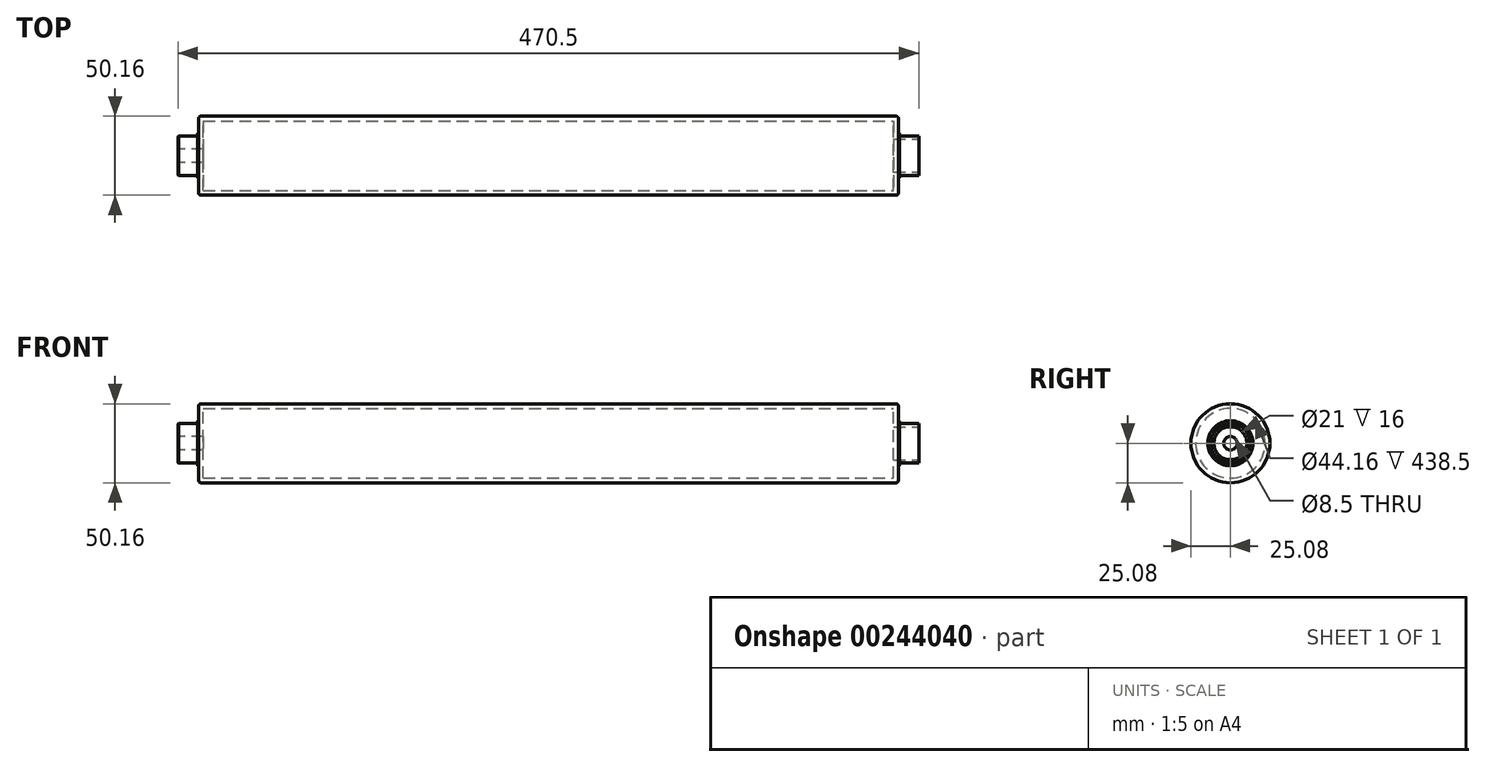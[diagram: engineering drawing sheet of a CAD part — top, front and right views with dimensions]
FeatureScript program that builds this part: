
annotation { "Feature Type Name" : "Feature", "Feature Type Description" : "" }
export const myFeature = defineFeature(function(context is Context, id is Id, definition is map)
    precondition{}
    {
        {
            var Q0;
            Q0=qCreatedBy(makeId("Front.planeOp"),FACE);
            var sketch = newSketch(context, id + "F0", { "sketchPlane" : qUnion([Q0])});
            skLineSegment(sketch, "E0", {"start": v(0, -12.5) * mm, "end": v(12.4, -12.5) * mm});
            skLineSegment(sketch, "E1", {"start": v(12.4, -12.5) * mm, "end": v(12.4, -14.3) * mm});
            skLineSegment(sketch, "E2", {"start": v(12.4, -14.3) * mm, "end": v(12.8, -14.3) * mm});
            skLineSegment(sketch, "E3", {"start": v(13, -14.5) * mm, "end": v(13, -23.58) * mm});
            skLineSegment(sketch, "E4", {"start": v(14.5, -25.08) * mm, "end": v(456, -25.08) * mm});
            skLineSegment(sketch, "E5", {"start": v(457.5, -23.58) * mm, "end": v(457.5, -14.5) * mm});
            skLineSegment(sketch, "E6", {"start": v(457.7, -14.3) * mm, "end": v(458.1, -14.3) * mm});
            skLineSegment(sketch, "E7", {"start": v(458.1, -14.3) * mm, "end": v(458.1, -12.5) * mm});
            skLineSegment(sketch, "E8", {"start": v(458.1, -12.5) * mm, "end": v(470.5, -12.5) * mm});
            skLineSegment(sketch, "E9", {"start": v(470.5, -12.5) * mm, "end": v(470.5, -10.5) * mm});
            skLineSegment(sketch, "E10", {"start": v(470.5, -10.5) * mm, "end": v(454.5, -10.5) * mm});
            skLineSegment(sketch, "E11", {"start": v(454.5, -10.5) * mm, "end": v(454.5, -22.08) * mm});
            skLineSegment(sketch, "E12", {"start": v(454.5, -22.08) * mm, "end": v(16, -22.08) * mm});
            skLineSegment(sketch, "E13", {"start": v(16, -22.08) * mm, "end": v(16, 0) * mm});
            skLineSegment(sketch, "E14", {"start": v(16, 0) * mm, "end": v(0, 0) * mm});
            skLineSegment(sketch, "E15", {"start": v(0, 0) * mm, "end": v(0, -12.5) * mm});
            skPoint(sketch, "E16.visualSharp", {"position": v(13, -14.3) * mm});
            skArc(sketch, "E16.filletArc", {"start": v(13, -14.5) * mm, "mid": v(12.94, -14.36) * mm, "end": v(12.8, -14.3) * mm});
            skPoint(sketch, "E17.visualSharp", {"position": v(13, -25.08) * mm});
            skArc(sketch, "E17.filletArc", {"start": v(13, -23.58) * mm, "mid": v(13.44, -24.64) * mm, "end": v(14.5, -25.08) * mm});
            skPoint(sketch, "E18.visualSharp", {"position": v(457.5, -25.08) * mm});
            skArc(sketch, "E18.filletArc", {"start": v(456, -25.08) * mm, "mid": v(457.06, -24.64) * mm, "end": v(457.5, -23.58) * mm});
            skPoint(sketch, "E19.visualSharp", {"position": v(457.5, -14.3) * mm});
            skArc(sketch, "E19.filletArc", {"start": v(457.7, -14.3) * mm, "mid": v(457.56, -14.36) * mm, "end": v(457.5, -14.5) * mm});
            skSolve(sketch);
        }
        {
            var Q0;
            Q0 = qSketchRegion(id + "F0", true);
            var Q1;
            Q1=sQuery(id+"F0.wireOp",EDGE,"E14");
            revolve(context, id + "F1", {"entities" : qUnion([Q0]), "axis" : qUnion([Q1]), "revolveType" : RevolveType.FULL});
        }
        {
            var Q0;
            Q0=makeQuery(id+"F1.opRevolve","SWEPT_EDGE",EDGE,{"disambiguationData":[OSD([sQuery(id+"F0.wireOp",EDGE,"E0"),sQuery(id+"F0.wireOp",EDGE,"E15")])]});
            chamfer(context, id + "F2", {"entities" : qUnion([Q0]), "chamferType" : ChamferType.OFFSET_ANGLE, "width" : .4 * mm, "oppositeDirection" : false, "angle" : 30 * degree, "tangentPropagation" : true});
        }
        {
            var Q0;
            Q0=makeQuery(id+"F1.opRevolve","SWEPT_FACE",FACE,{"disambiguationData":[OSD([sQuery(id+"F0.wireOp",EDGE,"E15")])]});
            var sketch = newSketch(context, id + "F3", { "sketchPlane" : qUnion([Q0])});
            skPoint(sketch, "E20", {"position": v(0, 0) * mm});
            skSolve(sketch);
        }
        {
            var Q0;
            Q0=sQuery(id+"F3.wireOp",VERTEX,"E20");
            var Q1;
            Q1=makeQuery(id+"F1.opRevolve","SWEPT_BODY",BODY,{"disambiguationData":[OSD([sQuery(id+"F0.wireOp",EDGE,"E0"),sQuery(id+"F0.wireOp",EDGE,"E1"),sQuery(id+"F0.wireOp",EDGE,"E2"),sQuery(id+"F0.wireOp",EDGE,"E3"),sQuery(id+"F0.wireOp",EDGE,"E4"),sQuery(id+"F0.wireOp",EDGE,"E5"),sQuery(id+"F0.wireOp",EDGE,"E6"),sQuery(id+"F0.wireOp",EDGE,"E7"),sQuery(id+"F0.wireOp",EDGE,"E8"),sQuery(id+"F0.wireOp",EDGE,"E9"),sQuery(id+"F0.wireOp",EDGE,"E10"),sQuery(id+"F0.wireOp",EDGE,"E11"),sQuery(id+"F0.wireOp",EDGE,"E12"),sQuery(id+"F0.wireOp",EDGE,"E13"),sQuery(id+"F0.wireOp",EDGE,"E14"),sQuery(id+"F0.wireOp",EDGE,"E15"),sQuery(id+"F0.wireOp",EDGE,"E16.filletArc"),sQuery(id+"F0.wireOp",EDGE,"E17.filletArc"),sQuery(id+"F0.wireOp",EDGE,"E18.filletArc"),sQuery(id+"F0.wireOp",EDGE,"E19.filletArc")])]});
            hole(context, id + "F4", {"style" : HoleStyle.SIMPLE, "endStyle" : HoleEndStyle.THROUGH, "standardTappedOrClearance" : lookupTablePath({ "standard" : "ISO", "engagement" : "75%", "pitch" : "1.5 mm", "size" : "M10", "type" : "Tapped" }), "standardBlindInLast" : lookupTablePath({ "standard" : "ISO", "engagement" : "75%", "pitch" : "1.5 mm", "size" : "M10", "type" : "Tapped" }), "holeDiameter" : 8.5 * mm, "locations" : qUnion([Q0]), "scope" : qUnion([Q1]), "isTappedThrough" : true, "majorDiameter" : 10 * mm, "showTappedDepth" : true});
        }
    });
